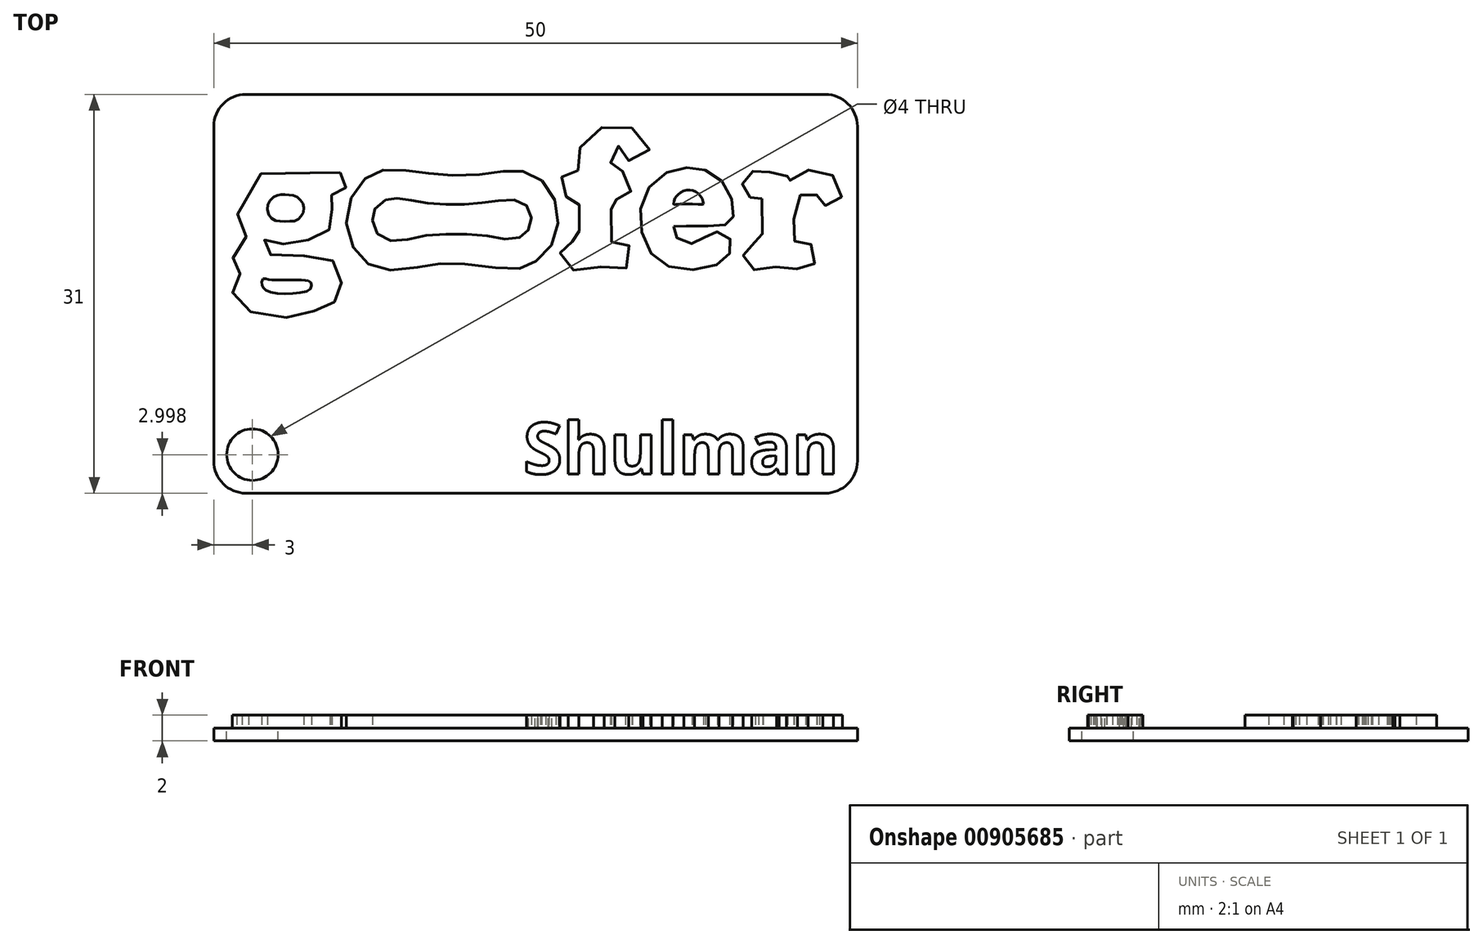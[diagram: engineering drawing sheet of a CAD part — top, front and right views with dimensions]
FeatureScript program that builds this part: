
annotation { "Feature Type Name" : "Feature", "Feature Type Description" : "" }
export const myFeature = defineFeature(function(context is Context, id is Id, definition is map)
    precondition{}
    {
        {
            var Q0;
            Q0=qCreatedBy(makeId("Top.planeOp"),FACE);
            var sketch = newSketch(context, id + "F0", { "sketchPlane" : qUnion([Q0])});
            skLineSegment(sketch, "E0", {"start": v(-25, 10.12) * mm, "end": v(25, -10.12) * mm, "construction": true});
            skFitSpline(sketch, "E1", {"points": [v(-15.17, 4.05) * mm, v(-17.41, 3.95) * mm, v(-17.57, 4.02) * mm, v(-21.96, 3.66) * mm, v(-23.01, 0.3) * mm, v(-22.28, -0.78) * mm, v(-22.75, -1.06) * mm, v(-23.48, -2.14) * mm, v(-23.28, -3.17) * mm, v(-22.81, -3.66) * mm, v(-23.14, -3.97) * mm, v(-23.47, -4.48) * mm, v(-23.5, -5.49) * mm, v(-22.86, -6.4) * mm, v(-21.05, -7.06) * mm, v(-18.81, -7.2) * mm, v(-17.48, -6.81) * mm, v(-16.54, -6.5) * mm, v(-15.78, -6.18) * mm, v(-15.37, -5.5) * mm, v(-15.08, -4.8) * mm, v(-15.15, -4.13) * mm, v(-15.52, -3.03) * mm, v(-16.57, -2.58) * mm, v(-18.2, -2.42) * mm, v(-20.3, -2.4) * mm, v(-21.2, -1.98) * mm, v(-21.18, -1.22) * mm, v(-20.86, -1.29) * mm, v(-20.26, -1.41) * mm, v(-19.4, -1.54) * mm, v(-18.11, -1.35) * mm, v(-17.39, -1.1) * mm, v(-16.4, -0.78) * mm, v(-15.87, 0) * mm, v(-15.87, 0.6) * mm, v(-15.8, 1.46) * mm, v(-15.87, 1.93) * mm, v(-15.96, 2.25) * mm, v(-15.74, 2.31) * mm, v(-15.24, 2.47) * mm, v(-14.82, 2.72) * mm, v(-14.7, 3.26) * mm, v(-14.89, 3.73) * mm, v(-15.17, 4.05) * mm]});
            skFitSpline(sketch, "E2", {"points": [v(-19.78, 2.32) * mm, v(-20.05, 2.28) * mm, v(-20.27, 2.19) * mm, v(-20.56, 1.94) * mm, v(-20.76, 1.63) * mm, v(-20.84, 1.3) * mm, v(-20.77, 0.8) * mm, v(-20.58, 0.54) * mm, v(-20.26, 0.33) * mm, v(-19.9, 0.25) * mm, v(-19.52, 0.24) * mm, v(-19.12, 0.25) * mm, v(-18.73, 0.28) * mm, v(-18.44, 0.4) * mm, v(-18.27, 0.6) * mm, v(-18.1, 0.84) * mm, v(-18, 1.18) * mm, v(-18.03, 1.5) * mm, v(-18.15, 1.75) * mm, v(-18.38, 2.02) * mm, v(-18.64, 2.22) * mm, v(-18.94, 2.29) * mm, v(-19.22, 2.3) * mm, v(-19.52, 2.32) * mm, v(-19.78, 2.32) * mm]});
            skFitSpline(sketch, "E3", {"points": [v(-21.18, -4.23) * mm, v(-21.27, -4.52) * mm, v(-21.2, -4.82) * mm, v(-21.04, -5.04) * mm, v(-20.19, -5.35) * mm, v(-18.44, -5.3) * mm, v(-17.5, -5.02) * mm, v(-17.42, -4.66) * mm, v(-17.55, -4.44) * mm, v(-17.8, -4.34) * mm, v(-18.18, -4.31) * mm, v(-20.1, -4.3) * mm, v(-20.67, -4.28) * mm, v(-20.93, -4.23) * mm, v(-21.18, -4.23) * mm]});
            skLineSegment(sketch, "E4.bottom", {"start": v(-25, 10.12) * mm, "end": v(25, 10.12) * mm});
            skLineSegment(sketch, "E4.top", {"start": v(-25, -10.12) * mm, "end": v(25, -10.12) * mm});
            skLineSegment(sketch, "E4.left", {"start": v(-25, 10.12) * mm, "end": v(-25, -10.12) * mm});
            skLineSegment(sketch, "E4.right", {"start": v(25, 10.12) * mm, "end": v(25, -10.12) * mm});
            skFitSpline(sketch, "E5", {"points": [v(-11.84, 4.24) * mm, v(-13.57, 3.25) * mm, v(-14.71, 0.5) * mm, v(-13.83, -2.27) * mm, v(-11.87, -3.5) * mm, v(-8.55, -3.23) * mm, v(-6.08, -3.01) * mm, v(-1.94, -3.44) * mm, v(-0.37, -3.1) * mm, v(1.25, -1.55) * mm, v(1.73, 0.94) * mm, v(0.61, 3.3) * mm, v(-1.27, 4.18) * mm, v(-3.37, 4) * mm, v(-6.72, 3.84) * mm, v(-9.3, 4.1) * mm, v(-11.84, 4.24) * mm]});
            skFitSpline(sketch, "E6", {"points": [v(-11.67, 1.93) * mm, v(-12.5, 1.17) * mm, v(-12.66, 0.3) * mm, v(-12.18, -0.84) * mm, v(-10.83, -1.29) * mm, v(-8.86, -0.9) * mm, v(-6.44, -0.75) * mm, v(-3.8, -0.88) * mm, v(-2, -1.15) * mm, v(-0.9, -0.84) * mm, v(-0.47, -0.21) * mm, v(-0.37, 0.83) * mm, v(-1, 1.7) * mm, v(-2.26, 1.92) * mm, v(-3.88, 1.72) * mm, v(-5.73, 1.57) * mm, v(-7.84, 1.62) * mm, v(-9.63, 1.87) * mm, v(-10.84, 2.05) * mm, v(-11.67, 1.93) * mm]});
            skFitSpline(sketch, "E7", {"points": [v(3.3, 4.2) * mm, v(2.85, 4.15) * mm, v(2.45, 4.11) * mm, v(1.94, 3.51) * mm, v(1.9, 2.81) * mm, v(2.36, 2.17) * mm, v(3.4, 1.93) * mm, v(3.37, 1.79) * mm, v(3.4, 1.62) * mm, v(3.4, 1.35) * mm, v(3.4, 0.9) * mm, v(3.4, -0.93) * mm, v(3.37, -1.26) * mm, v(3.3, -1.38) * mm, v(2.85, -1.33) * mm, v(2.47, -1.43) * mm, v(2.14, -1.67) * mm, v(1.9, -2.4) * mm, v(2.23, -3.26) * mm, v(3, -3.54) * mm, v(4.09, -3.33) * mm, v(5.4, -3.32) * mm, v(6.4, -3.52) * mm, v(7.23, -3.23) * mm, v(7.52, -2.22) * mm, v(7.1, -1.51) * mm, v(6.43, -1.33) * mm, v(6.04, -1.36) * mm, v(5.84, -1.32) * mm, v(5.84, -1.15) * mm, v(5.85, 1.56) * mm, v(5.82, 2.18) * mm, v(6.01, 2.1) * mm, v(6.34, 1.93) * mm, v(6.77, 1.93) * mm, v(7.18, 2.28) * mm, v(7.47, 2.8) * mm, v(7.29, 3.8) * mm, v(6.55, 4.16) * mm, v(5.83, 4.1) * mm, v(5.82, 4.36) * mm, v(5.83, 5.71) * mm, v(6.05, 6.04) * mm, v(6.46, 6.1) * mm, v(6.77, 5.99) * mm, v(6.88, 5.43) * mm, v(7.53, 4.84) * mm, v(8.63, 5.2) * mm, v(8.71, 6.46) * mm, v(7.77, 7.38) * mm, v(6.63, 7.65) * mm, v(5, 7.5) * mm, v(3.7, 6.57) * mm, v(3.38, 5.49) * mm, v(3.37, 4.44) * mm, v(3.3, 4.2) * mm]});
            skFitSpline(sketch, "E8", {"points": [v(10.72, -0.16) * mm, v(10.78, -0.74) * mm, v(11.47, -1.36) * mm, v(12.72, -1.37) * mm, v(13.32, -0.77) * mm, v(14.38, -0.61) * mm, v(15.16, -1.23) * mm, v(15.09, -2.22) * mm, v(14.06, -3.13) * mm, v(11.25, -3.49) * mm, v(9.15, -2.45) * mm, v(8.16, -0.22) * mm, v(8.45, 2.27) * mm, v(10.18, 4.03) * mm, v(12.05, 4.42) * mm, v(13.6, 4.06) * mm, v(15.02, 2.6) * mm, v(15.36, 0.95) * mm, v(15.2, 0.2) * mm, v(14.32, -0.1) * mm, v(12.65, -0.12) * mm, v(10.88, -0.13) * mm, v(10.72, -0.16) * mm]});
            skFitSpline(sketch, "E9", {"points": [v(10.9, 1.57) * mm, v(12.9, 1.56) * mm, v(13.03, 1.6) * mm, v(12.83, 2.2) * mm, v(12.3, 2.6) * mm, v(11.65, 2.66) * mm, v(11.04, 2.3) * mm, v(10.8, 1.93) * mm, v(10.74, 1.55) * mm, v(10.9, 1.57) * mm]});
            skFitSpline(sketch, "E10", {"points": [v(17.6, 2.02) * mm, v(17.6, -1.17) * mm, v(17.54, -1.38) * mm, v(17.07, -1.34) * mm, v(16.25, -1.87) * mm, v(16.28, -3) * mm, v(16.98, -3.52) * mm, v(18.27, -3.34) * mm, v(19.55, -3.32) * mm, v(20.72, -3.48) * mm, v(21.6, -3.14) * mm, v(21.74, -1.91) * mm, v(20.78, -1.34) * mm, v(20.17, -1.33) * mm, v(20.09, -0.52) * mm, v(20.14, 1.38) * mm, v(20.93, 2.53) * mm, v(21.8, 2.4) * mm, v(21.87, 1.92) * mm, v(22.4, 1.5) * mm, v(23.36, 1.58) * mm, v(23.82, 2.78) * mm, v(22.66, 4.06) * mm, v(21.03, 4.2) * mm, v(19.88, 3.6) * mm, v(19.6, 3.16) * mm, v(19.59, 3.4) * mm, v(19.44, 3.96) * mm, v(18.36, 4.07) * mm, v(17.27, 4.12) * mm, v(16.8, 4.14) * mm, v(16.15, 3.65) * mm, v(16.15, 2.55) * mm, v(16.53, 2.16) * mm, v(17.33, 2) * mm, v(17.48, 2.03) * mm, v(17.6, 2.02) * mm]});
            skSolve(sketch);
        }
        {
            var Q0;
            Q0=qCreatedBy(makeId("Top.planeOp"),FACE);
            var sketch = newSketch(context, id + "F1", { "sketchPlane" : qUnion([Q0])});
            skLineSegment(sketch, "E11.bottom", {"start": v(-25, -20.88) * mm, "end": v(25, -20.88) * mm});
            skLineSegment(sketch, "E11.top", {"start": v(-25, 10.12) * mm, "end": v(25, 10.12) * mm});
            skLineSegment(sketch, "E11.left", {"start": v(-25, -20.88) * mm, "end": v(-25, 10.12) * mm});
            skLineSegment(sketch, "E11.right", {"start": v(25, -20.88) * mm, "end": v(25, 10.12) * mm});
            skPoint(sketch, "E11.middle", {"position": v(0, -5.38) * mm});
            skSolve(sketch);
        }
        {
            var Q0;
            Q0=qCreatedBy(makeId("Top.planeOp"),FACE);
            var sketch = newSketch(context, id + "F2", { "sketchPlane" : qUnion([Q0])});
            skText(sketch, "E12", { "text": "Shulman", "fontName": "OpenSans-Bold.ttf"});
            const initialGuessF2  = {"E12": [-0.00096, -0.01938, 1, 0, 0.004]};
            skSetInitialGuess(sketch, initialGuessF2);
            skSolve(sketch);
        }
        {
            var Q0;
            Q0=makeQuery(id+"F1.imprint","IMPRINT",FACE,{"disambiguationData":[TD([[makeQuery(id+"F1.imprint","IMPRINT",EDGE,{"derivedFrom":sQuery(id+"F1.wireOp",EDGE,"E11.bottom")}),1.0]])]});
            extrude(context, id + "F3", {"entities" : qUnion([Q0]), "oppositeDirection" : true, "depth" : 1 * mm, "offsetDistance" : 25 * mm});
        }
        {
            var Q0;
            Q0=makeQuery(id+"F0.imprint","IMPRINT",FACE,{"disambiguationData":[TD([[makeQuery(id+"F0.imprint","IMPRINT",EDGE,{"derivedFrom":sQuery(id+"F0.wireOp",EDGE,"E1")}),1.0]])]});
            var Q1;
            Q1=makeQuery(id+"F0.imprint","IMPRINT",FACE,{"disambiguationData":[TD([[makeQuery(id+"F0.imprint","IMPRINT",EDGE,{"derivedFrom":sQuery(id+"F0.wireOp",EDGE,"E5")}),1.0]])]});
            var Q2;
            Q2=makeQuery(id+"F0.imprint","IMPRINT",FACE,{"disambiguationData":[TD([[makeQuery(id+"F0.imprint","IMPRINT",EDGE,{"derivedFrom":sQuery(id+"F0.wireOp",EDGE,"E7")}),1.0]])]});
            var Q3;
            Q3=makeQuery(id+"F0.imprint","IMPRINT",FACE,{"disambiguationData":[TD([[makeQuery(id+"F0.imprint","IMPRINT",EDGE,{"derivedFrom":sQuery(id+"F0.wireOp",EDGE,"E8")}),-1.0]])]});
            var Q4;
            Q4=makeQuery(id+"F0.imprint","IMPRINT",FACE,{"disambiguationData":[TD([[makeQuery(id+"F0.imprint","IMPRINT",EDGE,{"derivedFrom":sQuery(id+"F0.wireOp",EDGE,"E10")}),1.0]])]});
            var Q5;
            Q5 = qSketchRegion(id + "F2", true);
            extrude(context, id + "F4", {"entities" : qUnion([Q0, Q1, Q2, Q3, Q4, Q5]), "operationType" : NewBodyOperationType.ADD, "depth" : 1 * mm, "offsetDistance" : 25 * mm});
        }
        {
            var Q0;
            {var subQ0=sQuery(id+"F1.wireOp",EDGE,"E11.bottom");var subQ1=sQuery(id+"F1.wireOp",EDGE,"E11.right");var subQ2=sQuery(id+"F1.wireOp",EDGE,"E11.top");var subQ3=sQuery(id+"F1.wireOp",EDGE,"E11.left");Q0=makeQuery(id+"F4.boolean.opBoolean","SPLIT",FACE,{"disambiguationData":[TD([makeQuery(id+"F3.opExtrude","SWEPT_FACE",FACE,{"disambiguationData":[OSD([subQ0])]})])],"derivedFrom":makeQuery(id+"F3.opExtrude","CAP_FACE",FACE,{"disambiguationData":[OSD([subQ0,subQ2,subQ3,subQ1])],"isStart":true})});}
            var sketch = newSketch(context, id + "F5", { "sketchPlane" : qUnion([Q0])});
            skCircle(sketch, "E13", {"center": v(-22, -17.88) * mm, "radius": 2 * mm});
            skSolve(sketch);
        }
        {
            var Q0;
            Q0=makeQuery(id+"F5.imprint","IMPRINT",FACE,{"disambiguationData":[TD([[makeQuery(id+"F5.imprint","IMPRINT",EDGE,{"derivedFrom":sQuery(id+"F5.wireOp",EDGE,"E13")}),1.0]])]});
            var Q1;
            Q1=makeQuery(id+"F3.opExtrude","CAP_FACE",FACE,{"disambiguationData":[OSD([sQuery(id+"F1.wireOp",EDGE,"E11.bottom"),sQuery(id+"F1.wireOp",EDGE,"E11.top"),sQuery(id+"F1.wireOp",EDGE,"E11.left"),sQuery(id+"F1.wireOp",EDGE,"E11.right")])],"isStart":false});
            extrude(context, id + "F6", {"entities" : qUnion([Q0]), "operationType" : NewBodyOperationType.REMOVE, "endBound" : BoundingType.UP_TO_SURFACE, "oppositeDirection" : true, "depth" : 25 * mm, "endBoundEntityFace" : qUnion([Q1]), "offsetDistance" : 25 * mm});
        }
        {
            var Q0;
            Q0=makeQuery(id+"F3.opExtrude","SWEPT_EDGE",EDGE,{"disambiguationData":[OSD([sQuery(id+"F1.wireOp",EDGE,"E11.top"),sQuery(id+"F1.wireOp",EDGE,"E11.left")])]});
            var Q1;
            Q1=makeQuery(id+"F3.opExtrude","SWEPT_EDGE",EDGE,{"disambiguationData":[OSD([sQuery(id+"F1.wireOp",EDGE,"E11.top"),sQuery(id+"F1.wireOp",EDGE,"E11.right")])]});
            var Q2;
            Q2=makeQuery(id+"F3.opExtrude","SWEPT_EDGE",EDGE,{"disambiguationData":[OSD([sQuery(id+"F1.wireOp",EDGE,"E11.bottom"),sQuery(id+"F1.wireOp",EDGE,"E11.left")])]});
            var Q3;
            Q3=makeQuery(id+"F3.opExtrude","SWEPT_EDGE",EDGE,{"disambiguationData":[OSD([sQuery(id+"F1.wireOp",EDGE,"E11.bottom"),sQuery(id+"F1.wireOp",EDGE,"E11.right")])]});
            fillet(context, id + "F7", {"entities" : qUnion([Q0, Q1, Q2, Q3]), "radius" : 2.5 * mm, "tangentPropagation" : true, "allowEdgeOverflow" : false});
        }
    });
